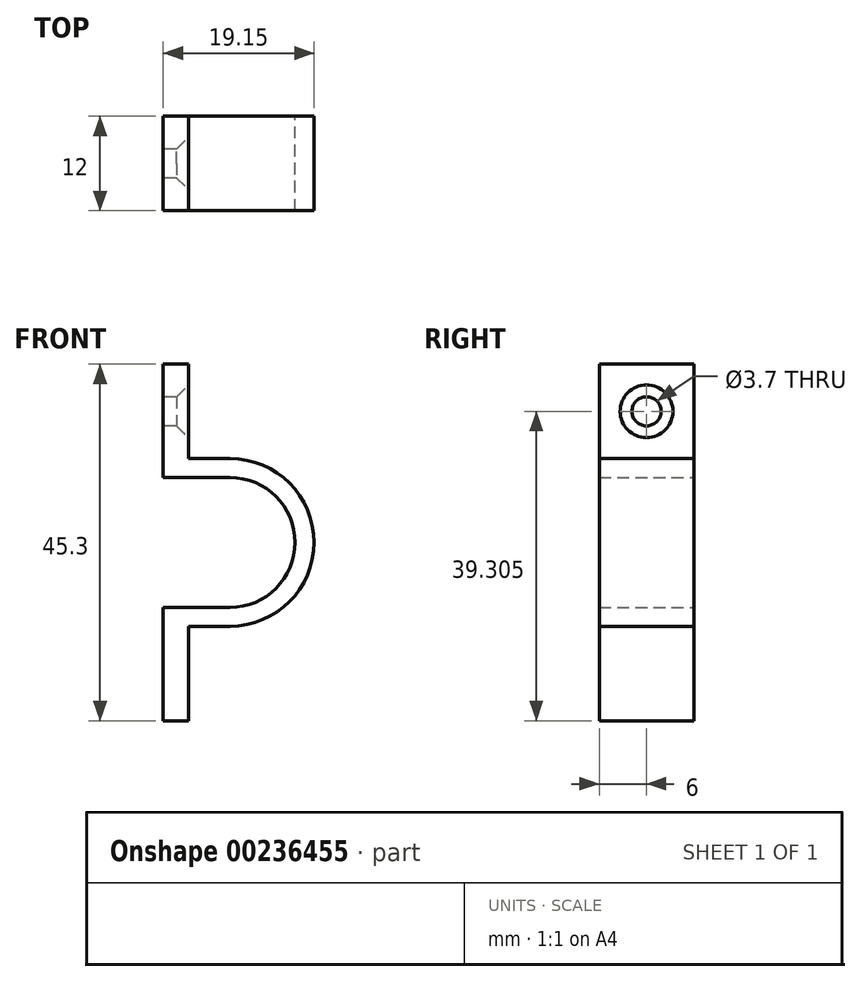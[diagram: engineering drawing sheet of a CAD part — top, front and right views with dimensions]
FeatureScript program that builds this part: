
annotation { "Feature Type Name" : "Feature", "Feature Type Description" : "" }
export const myFeature = defineFeature(function(context is Context, id is Id, definition is map)
    precondition{}
    {
        {
            var Q0;
            Q0=qCreatedBy(makeId("Front.planeOp"),FACE);
            var sketch = newSketch(context, id + "F0", { "sketchPlane" : qUnion([Q0])});
            skLineSegment(sketch, "E0.bottom", {"start": v(-39.03, 42) * mm, "end": v(-35.83, 42) * mm});
            skLineSegment(sketch, "E0.top", {"start": v(-39.03, -3.3) * mm, "end": v(-35.83, -3.3) * mm});
            skLineSegment(sketch, "E0.left", {"start": v(-39.03, 42) * mm, "end": v(-39.03, 27.6) * mm});
            skLineSegment(sketch, "E0.right", {"start": v(-35.83, 42) * mm, "end": v(-35.83, 30) * mm});
            skLineSegment(sketch, "E1.trimOffspring", {"start": v(-35.83, 8.7) * mm, "end": v(-35.83, -3.3) * mm});
            skLineSegment(sketch, "E2.trimOffspring", {"start": v(-39.03, 11.1) * mm, "end": v(-39.03, -3.3) * mm});
            skLineSegment(sketch, "E3", {"start": v(-35.83, 30) * mm, "end": v(-30.53, 30) * mm});
            skLineSegment(sketch, "E4", {"start": v(-30.53, 27.6) * mm, "end": v(-39.03, 27.6) * mm});
            skLineSegment(sketch, "E5", {"start": v(-39.03, 11.1) * mm, "end": v(-30.53, 11.1) * mm});
            skLineSegment(sketch, "E6", {"start": v(-30.53, 8.7) * mm, "end": v(-35.83, 8.7) * mm});
            skLineSegment(sketch, "E7", {"start": v(-30.53, 27.6) * mm, "end": v(-30.53, 11.1) * mm, "construction": true});
            skArc(sketch, "E8", {"start": v(-30.53, 11.1) * mm, "mid": v(-22.28, 19.34) * mm, "end": v(-30.53, 27.6) * mm});
            skArc(sketch, "E9", {"start": v(-30.53, 8.7) * mm, "mid": v(-19.88, 19.34) * mm, "end": v(-30.53, 30) * mm});
            skSolve(sketch);
        }
        {
            var Q0;
            Q0=makeQuery(id+"F0.imprint","IMPRINT",FACE,{"disambiguationData":[TD([[makeQuery(id+"F0.imprint","IMPRINT",EDGE,{"derivedFrom":sQuery(id+"F0.wireOp",EDGE,"E0.bottom")}),-1.0]])]});
            extrude(context, id + "F1", {"entities" : qUnion([Q0]), "depth" : 12 * mm});
        }
        {
            var Q0;
            Q0=makeQuery(id+"F1.opExtrude","SWEPT_FACE",FACE,{"disambiguationData":[OSD([sQuery(id+"F0.wireOp",EDGE,"E0.left")])]});
            var sketch = newSketch(context, id + "F2", { "sketchPlane" : qUnion([Q0])});
            skCircle(sketch, "E10", {"center": v(6, 36) * mm, "radius": 1.85 * mm});
            skLineSegment(sketch, "E11.0.0", {"start": v(0, 11.1) * mm, "end": v(0, 27.6) * mm, "construction": true});
            skLineSegment(sketch, "E11.0.1", {"start": v(0, 11.1) * mm, "end": v(12, 11.1) * mm, "construction": true});
            skLineSegment(sketch, "E11.0.2", {"start": v(12, 11.1) * mm, "end": v(12, 27.6) * mm, "construction": true});
            skLineSegment(sketch, "E11.0.3", {"start": v(12, 27.6) * mm, "end": v(0, 27.6) * mm, "construction": true});
            skLineSegment(sketch, "E12", {"start": v(0, 19.34) * mm, "end": v(12, 19.34) * mm, "construction": true});
            skCircle(sketch, "E13.MirrorC", {"center": v(6, 2.7) * mm, "radius": 1.85 * mm});
            skSolve(sketch);
        }
        {
            var Q0;
            Q0=makeQuery(id+"F2.imprint","IMPRINT",FACE,{"disambiguationData":[TD([[makeQuery(id+"F2.imprint","IMPRINT",EDGE,{"derivedFrom":sQuery(id+"F2.wireOp",EDGE,"E10")}),1.0]])]});
            var Q1;
            Q1=makeQuery(id+"F2.imprint","IMPRINT",FACE,{"disambiguationData":[TD([[makeQuery(id+"F2.imprint","IMPRINT",EDGE,{"derivedFrom":sQuery(id+"F2.wireOp",EDGE,"E13.MirrorC")}),-1.0]])]});
            extrude(context, id + "F3", {"entities" : qUnion([Q0, Q1]), "operationType" : NewBodyOperationType.REMOVE, "endBound" : BoundingType.THROUGH_ALL, "oppositeDirection" : true, "depth" : 25 * mm});
        }
        {
            var Q0;
            Q0=makeQuery(id+"F3.boolean.opBoolean","INTERSECT",EDGE,{"derivedFrom":[makeQuery(id+"F1.opExtrude","SWEPT_FACE",FACE,{"disambiguationData":[OSD([sQuery(id+"F0.wireOp",EDGE,"E0.right")])]}),makeQuery(id+"F3.opExtrude","SWEPT_FACE",FACE,{"disambiguationData":[OSD([sQuery(id+"F2.wireOp",EDGE,"E10")])]})]});
            var Q1;
            Q1=makeQuery(id+"F3.boolean.opBoolean","INTERSECT",EDGE,{"derivedFrom":[makeQuery(id+"F1.opExtrude","SWEPT_FACE",FACE,{"disambiguationData":[OSD([sQuery(id+"F0.wireOp",EDGE,"E1.trimOffspring")])]}),makeQuery(id+"F3.opExtrude","SWEPT_FACE",FACE,{"disambiguationData":[OSD([sQuery(id+"F2.wireOp",EDGE,"E13.MirrorC")])]})]});
            chamfer(context, id + "F4", {"entities" : qUnion([Q0, Q1]), "width" : 1.5 * mm, "tangentPropagation" : true});
        }
    });
